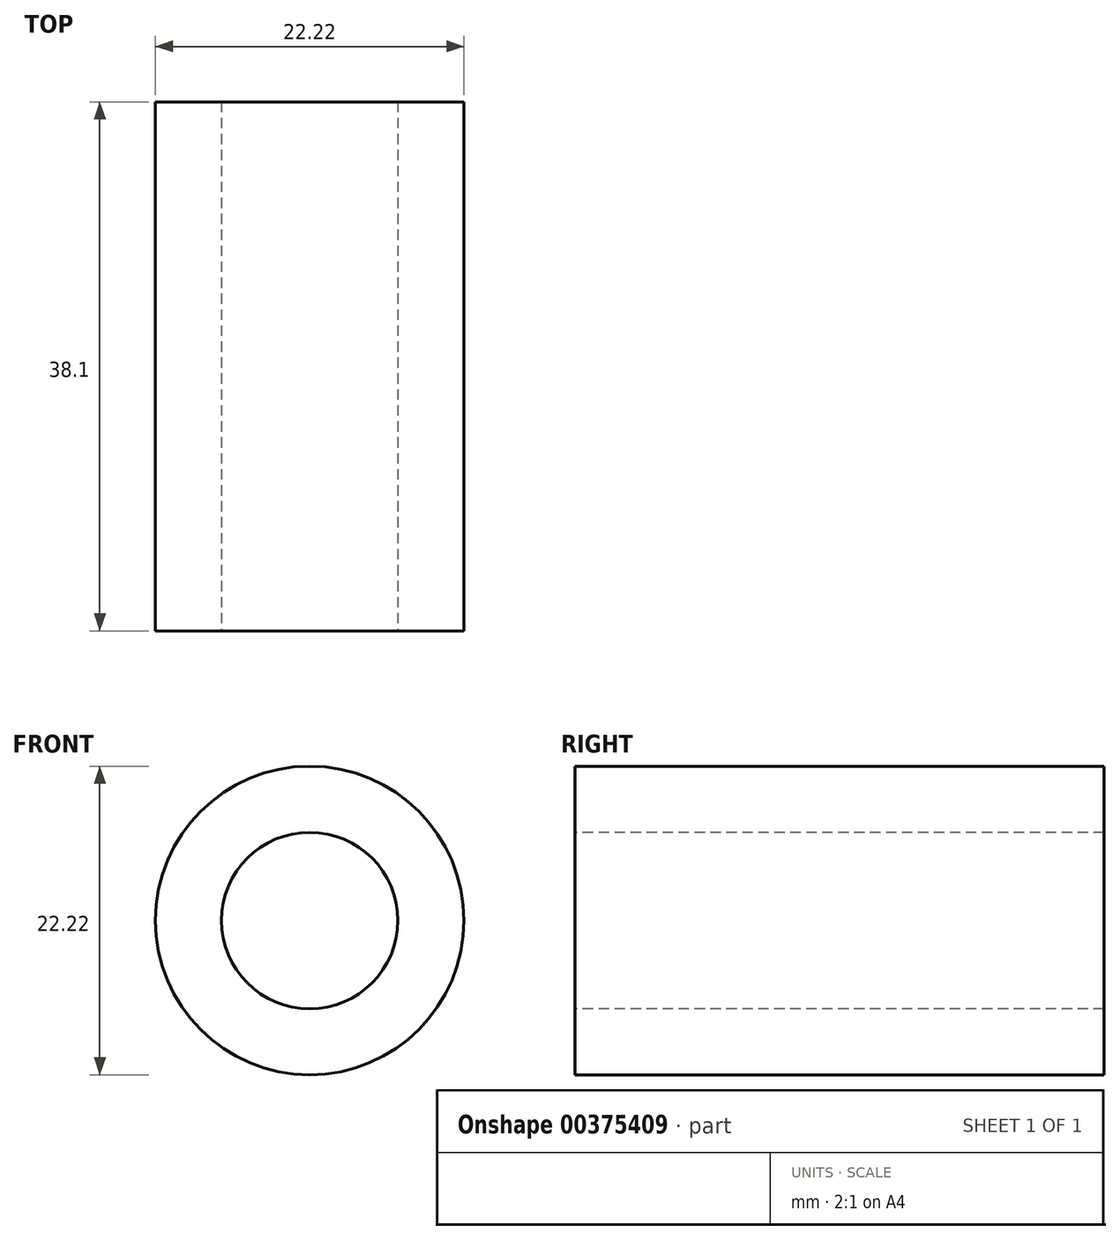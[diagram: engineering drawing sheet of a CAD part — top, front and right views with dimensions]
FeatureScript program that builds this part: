
annotation { "Feature Type Name" : "Feature", "Feature Type Description" : "" }
export const myFeature = defineFeature(function(context is Context, id is Id, definition is map)
    precondition{}
    {
        {
            var Q0;
            Q0=qCreatedBy(makeId("Front.planeOp"),FACE);
            var sketch = newSketch(context, id + "F0", { "sketchPlane" : qUnion([Q0])});
            skCircle(sketch, "E0", {"center": v(0, 0) * mm, "radius": 11.11 * mm});
            skSolve(sketch);
        }
        {
            var Q0;
            Q0=qSketchRegion(id+"F0",true);
            extrude(context, id + "F1", {"entities" : qUnion([Q0]), "depth" : 38.1 * mm, "symmetric" : true});
        }
        {
            var Q0;
            Q0=makeQuery(id+"F1.opExtrude","CAP_FACE",FACE,{"disambiguationData":[OSD([sQuery(id+"F0.wireOp",EDGE,"E0")])],"isStart":false});
            var sketch = newSketch(context, id + "F2", { "sketchPlane" : qUnion([Q0])});
            skCircle(sketch, "E1", {"center": v(0, 0) * mm, "radius": 6.35 * mm});
            skSolve(sketch);
        }
        {
            var Q0;
            Q0=qSketchRegion(id+"F2",true);
            extrude(context, id + "F3", {"entities" : qUnion([Q0]), "operationType" : NewBodyOperationType.REMOVE, "endBound" : BoundingType.THROUGH_ALL, "oppositeDirection" : true, "depth" : 25.4 * mm});
        }
    });
